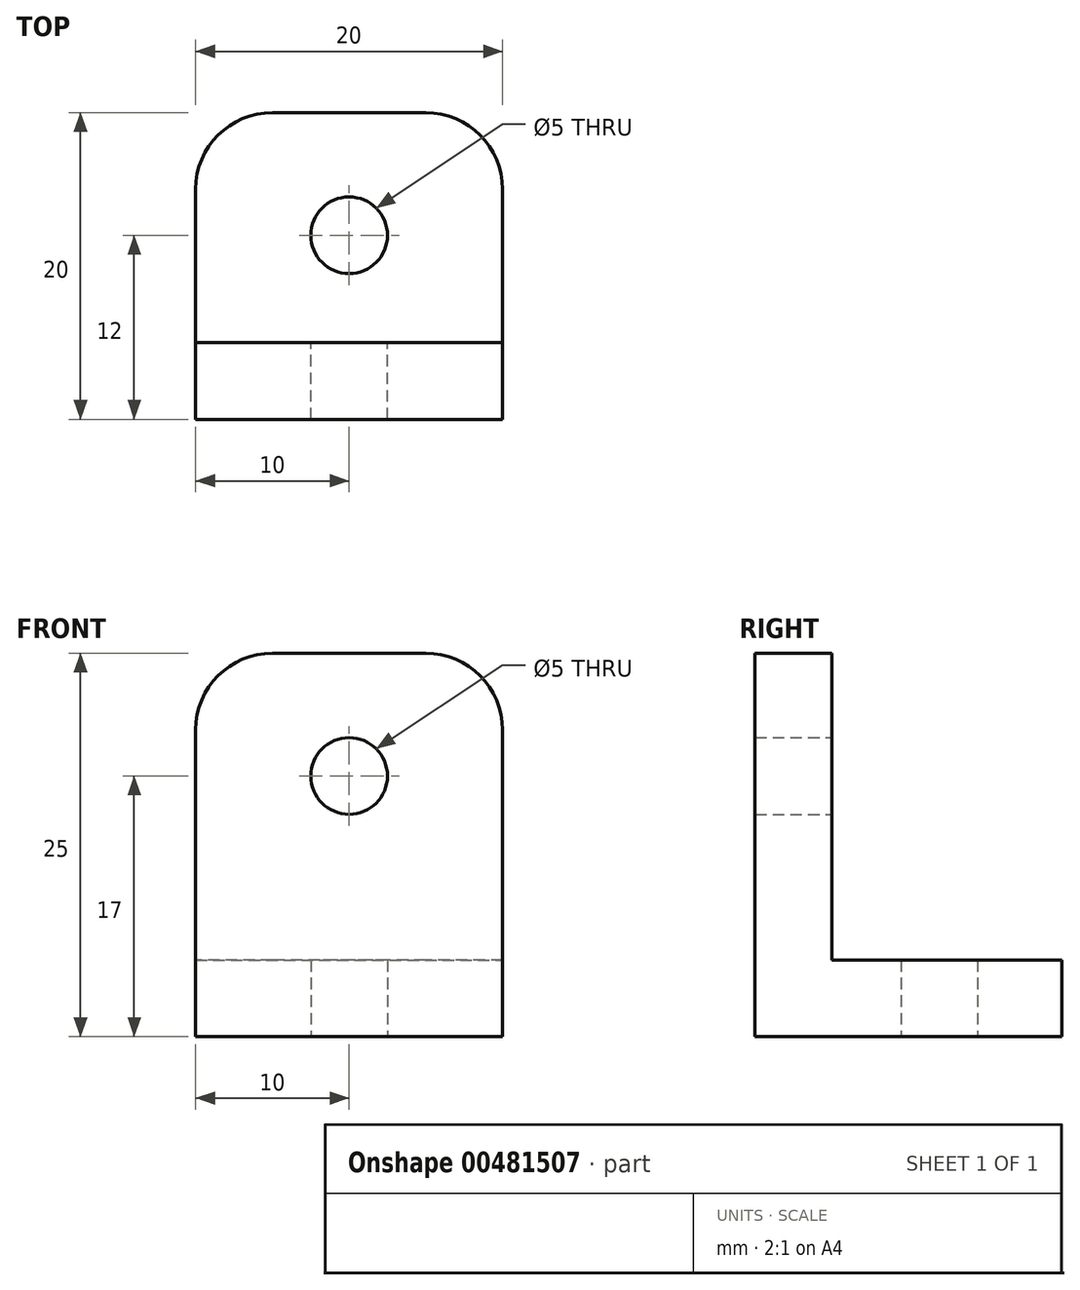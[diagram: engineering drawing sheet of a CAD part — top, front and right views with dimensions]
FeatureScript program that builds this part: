
annotation { "Feature Type Name" : "Feature", "Feature Type Description" : "" }
export const myFeature = defineFeature(function(context is Context, id is Id, definition is map)
    precondition{}
    {
        {
            var Q0;
            Q0=qCreatedBy(makeId("Top.planeOp"),FACE);
            var sketch = newSketch(context, id + "F0", { "sketchPlane" : qUnion([Q0])});
            skLineSegment(sketch, "E0.bottom", {"start": v(10, -10) * mm, "end": v(-10, -10) * mm});
            skLineSegment(sketch, "E0.top", {"start": v(10, 10) * mm, "end": v(-10, 10) * mm});
            skLineSegment(sketch, "E0.left", {"start": v(10, -10) * mm, "end": v(10, 10) * mm});
            skLineSegment(sketch, "E0.right", {"start": v(-10, -10) * mm, "end": v(-10, 10) * mm});
            skPoint(sketch, "E0.middle", {"position": v(0, 0) * mm});
            skCircle(sketch, "E1", {"center": v(0, 2) * mm, "radius": 2.5 * mm});
            skLineSegment(sketch, "E2", {"start": v(0, 10) * mm, "end": v(0, 0) * mm, "construction": true});
            skSolve(sketch);
        }
        {
            var Q0;
            Q0=makeQuery(id+"F0.imprint","IMPRINT",FACE,{"disambiguationData":[TD([[makeQuery(id+"F0.imprint","IMPRINT",EDGE,{"derivedFrom":sQuery(id+"F0.wireOp",EDGE,"E0.bottom")}),-1.0]])]});
            extrude(context, id + "F1", {"entities" : qUnion([Q0]), "depth" : 5 * mm});
        }
        {
            var Q0;
            Q0=makeQuery(id+"F1.opExtrude","CAP_FACE",FACE,{"disambiguationData":[OSD([sQuery(id+"F0.wireOp",EDGE,"E0.bottom"),sQuery(id+"F0.wireOp",EDGE,"E0.top"),sQuery(id+"F0.wireOp",EDGE,"E0.left"),sQuery(id+"F0.wireOp",EDGE,"E0.right")])],"isStart":false});
            var sketch = newSketch(context, id + "F2", { "sketchPlane" : qUnion([Q0])});
            skLineSegment(sketch, "E3.bottom", {"start": v(-10, -10) * mm, "end": v(10, -10) * mm});
            skLineSegment(sketch, "E3.top", {"start": v(-10, -5) * mm, "end": v(10, -5) * mm});
            skLineSegment(sketch, "E3.left", {"start": v(-10, -10) * mm, "end": v(-10, -5) * mm});
            skLineSegment(sketch, "E3.right", {"start": v(10, -10) * mm, "end": v(10, -5) * mm});
            skSolve(sketch);
        }
        {
            var Q0;
            Q0=makeQuery(id+"F2.imprint","IMPRINT",FACE,{"disambiguationData":[TD([[makeQuery(id+"F2.imprint","IMPRINT",EDGE,{"derivedFrom":sQuery(id+"F2.wireOp",EDGE,"E3.bottom")}),-1.0]])]});
            extrude(context, id + "F3", {"entities" : qUnion([Q0]), "operationType" : NewBodyOperationType.ADD, "depth" : 20 * mm});
        }
        {
            var Q0;
            Q0=makeQuery(id+"F3.opExtrude","SWEPT_FACE",FACE,{"disambiguationData":[OSD([sQuery(id+"F2.wireOp",EDGE,"E3.top")])]});
            var sketch = newSketch(context, id + "F4", { "sketchPlane" : qUnion([Q0])});
            skCircle(sketch, "E4", {"center": v(0, 17) * mm, "radius": 2.5 * mm});
            skPoint(sketch, "E4.centerSnap0", {"position": v(0, 25) * mm});
            skSolve(sketch);
        }
        {
            var Q0;
            Q0=makeQuery(id+"F4.imprint","IMPRINT",FACE,{"disambiguationData":[TD([[makeQuery(id+"F4.imprint","IMPRINT",EDGE,{"derivedFrom":sQuery(id+"F4.wireOp",EDGE,"E4")}),1.0]])]});
            extrude(context, id + "F5", {"entities" : qUnion([Q0]), "operationType" : NewBodyOperationType.REMOVE, "endBound" : BoundingType.THROUGH_ALL, "oppositeDirection" : true, "depth" : 26 * mm});
        }
        {
            var Q0;
            Q0=makeQuery(id+"F3.opExtrude","CAP_EDGE",EDGE,{"disambiguationData":[OSD([sQuery(id+"F2.wireOp",EDGE,"E3.left")])],"isStart":false});
            var Q1;
            Q1=makeQuery(id+"F3.opExtrude","CAP_EDGE",EDGE,{"disambiguationData":[OSD([sQuery(id+"F2.wireOp",EDGE,"E3.right")])],"isStart":false});
            var Q2;
            Q2=makeQuery(id+"F1.opExtrude","SWEPT_EDGE",EDGE,{"disambiguationData":[OSD([sQuery(id+"F0.wireOp",EDGE,"E0.top"),sQuery(id+"F0.wireOp",EDGE,"E0.left")])]});
            var Q3;
            Q3=makeQuery(id+"F1.opExtrude","SWEPT_EDGE",EDGE,{"disambiguationData":[OSD([sQuery(id+"F0.wireOp",EDGE,"E0.top"),sQuery(id+"F0.wireOp",EDGE,"E0.right")])]});
            fillet(context, id + "F6", {"entities" : qUnion([Q0, Q1, Q2, Q3]), "radius" : 5 * mm, "tangentPropagation" : true, "allowEdgeOverflow" : false});
        }
    });
